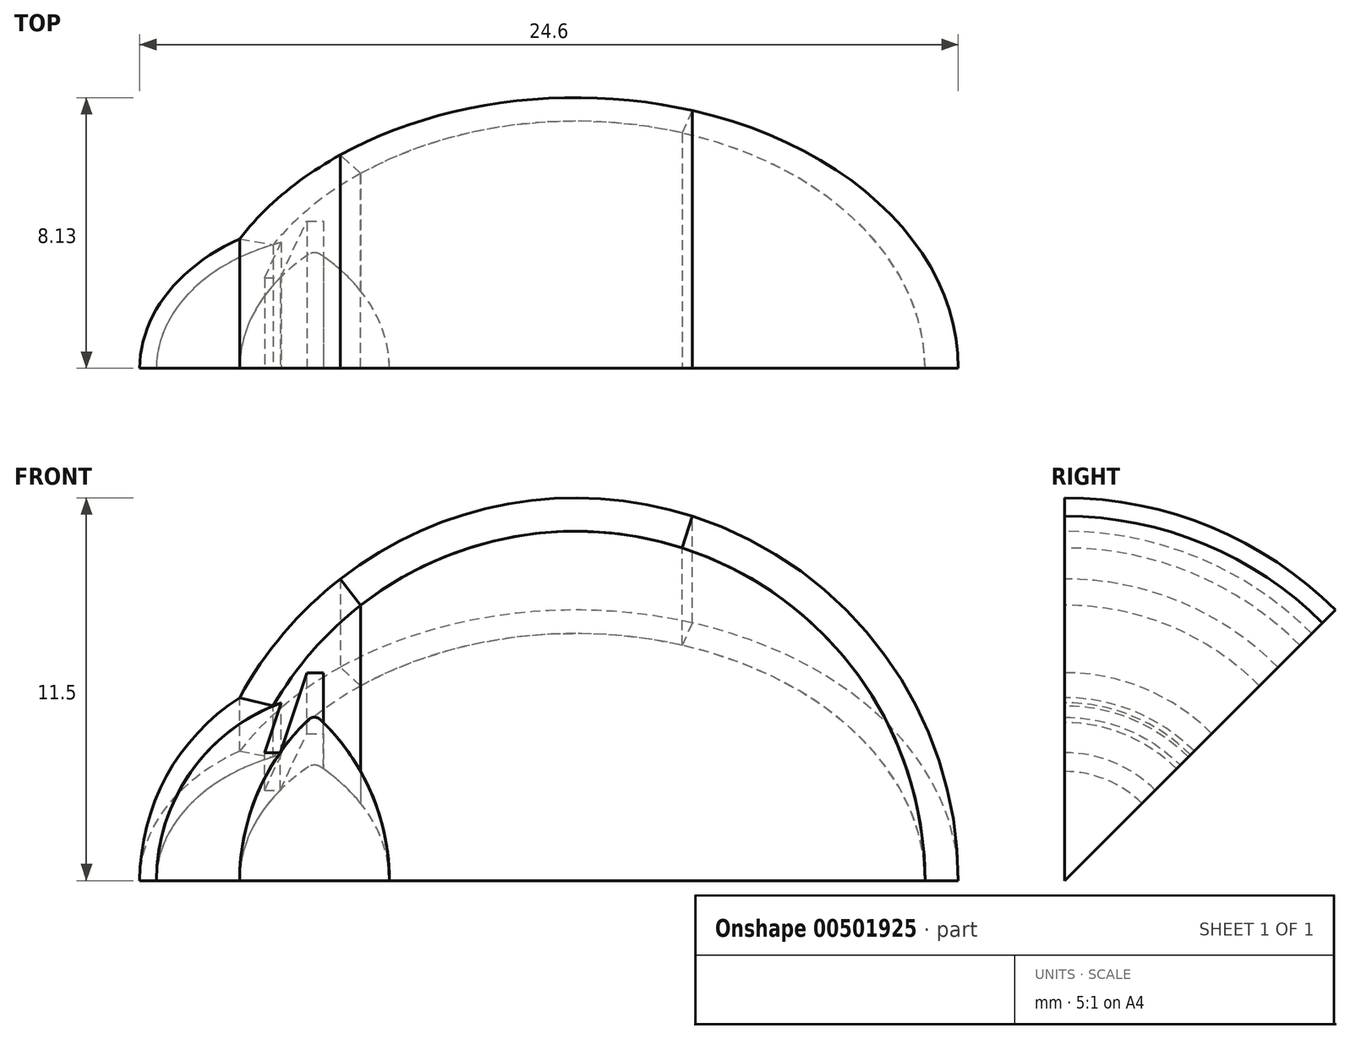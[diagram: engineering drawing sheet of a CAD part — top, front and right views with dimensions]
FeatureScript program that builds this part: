
annotation { "Feature Type Name" : "Feature", "Feature Type Description" : "" }
export const myFeature = defineFeature(function(context is Context, id is Id, definition is map)
    precondition{}
    {
        {
            var Q0;
            Q0=qCreatedBy(makeId("Front.planeOp"),FACE);
            var sketch = newSketch(context, id + "F0", { "sketchPlane" : qUnion([Q0])});
            skArc(sketch, "E0", {"start": v(11.5, 0) * mm, "mid": v(2.84, 11.14) * mm, "end": v(-10.1, 5.5) * mm});
            skLineSegment(sketch, "E1", {"start": v(11.5, 0) * mm, "end": v(-11.5, 0) * mm});
            skArc(sketch, "E2", {"start": v(-10.1, 5.5) * mm, "mid": v(-12.3, 3.13) * mm, "end": v(-13.1, 0) * mm});
            skLineSegment(sketch, "E3", {"start": v(-11.5, 0) * mm, "end": v(-13.1, 0) * mm});
            skSolve(sketch);
        }
        {
            var Q0;
            Q0=qSketchRegion(id+"F0",true);
            var Q1;
            Q1=sQuery(id+"F0.wireOp",EDGE,"E1");
            revolve(context, id + "F1", {"entities" : qUnion([Q0]), "axis" : qUnion([Q1]), "revolveType" : RevolveType.ONE_DIRECTION, "angle" : 45 * degree});
        }
        {
            var Q0;
            Q0=qCreatedBy(makeId("Front.planeOp"),FACE);
            var sketch = newSketch(context, id + "F2", { "sketchPlane" : qUnion([Q0])});
            skLineSegment(sketch, "E4", {"start": v(-10.1, 5.5) * mm, "end": v(-9.1, 5.25) * mm});
            skLineSegment(sketch, "E5", {"start": v(11.5, 0) * mm, "end": v(10.5, 0) * mm});
            skArc(sketch, "E6", {"start": v(10.5, 0) * mm, "mid": v(2.72, 10.14) * mm, "end": v(-9.1, 5.25) * mm});
            skArc(sketch, "E7", {"start": v(11.5, 0) * mm, "mid": v(2.84, 11.14) * mm, "end": v(-10.1, 5.5) * mm});
            skSolve(sketch);
        }
        {
            var Q0;
            Q0=makeQuery(id+"F2.imprint","IMPRINT",FACE,{"disambiguationData":[TD([[makeQuery(id+"F2.imprint","IMPRINT",EDGE,{"derivedFrom":sQuery(id+"F2.wireOp",EDGE,"E4")}),1.0]])]});
            var Q1;
            Q1=sQuery(id+"F2.wireOp",EDGE,"E6");
            var Q2;
            Q2=sQuery(id+"F2.wireOp",EDGE,"E4");
            var Q3;
            Q3=sQuery(id+"F0.wireOp",EDGE,"E1");
            revolve(context, id + "F3", {"operationType" : NewBodyOperationType.REMOVE, "entities" : qUnion([Q0]), "surfaceEntities" : qUnion([Q1, Q2]), "axis" : qUnion([Q3]), "revolveType" : RevolveType.ONE_DIRECTION, "angle" : 45 * degree});
        }
        {
            var Q0;
            Q0=qSketchRegion(id+"F2",true);
            var Q1;
            Q1=sQuery(id+"F0.wireOp",EDGE,"E1");
            revolve(context, id + "F4", {"entities" : qUnion([Q0]), "axis" : qUnion([Q1]), "revolveType" : RevolveType.ONE_DIRECTION, "angle" : 45 * degree});
        }
        {
            var Q0;
            Q0=makeQuery(id+"F0.imprint","IMPRINT",FACE,{"disambiguationData":[TD([[makeQuery(id+"F0.imprint","IMPRINT",EDGE,{"derivedFrom":sQuery(id+"F0.wireOp",EDGE,"E0")}),1.0]])]});
            var sketch = newSketch(context, id + "F5", { "sketchPlane" : qUnion([Q0])});
            skArc(sketch, "E8", {"start": v(-9.1, 5.25) * mm, "mid": v(-11.64, 3.16) * mm, "end": v(-12.6, 0) * mm});
            skLineSegment(sketch, "E9", {"start": v(-10.1, 5.5) * mm, "end": v(-9.1, 5.25) * mm});
            skLineSegment(sketch, "E10", {"start": v(-13.1, 0) * mm, "end": v(-12.6, 0) * mm});
            skArc(sketch, "E11", {"start": v(-10.1, 5.5) * mm, "mid": v(-12.3, 3.13) * mm, "end": v(-13.1, 0) * mm});
            skSolve(sketch);
        }
        {
            var Q0;
            Q0=qSketchRegion(id+"F5",true);
            var Q1;
            Q1=sQuery(id+"F5.wireOp",EDGE,"E8");
            var Q2;
            Q2=sQuery(id+"F5.wireOp",EDGE,"E9");
            var Q3;
            Q3=sQuery(id+"F0.wireOp",EDGE,"E3");
            revolve(context, id + "F6", {"operationType" : NewBodyOperationType.REMOVE, "entities" : qUnion([Q0]), "surfaceEntities" : qUnion([Q1, Q2]), "axis" : qUnion([Q3]), "revolveType" : RevolveType.ONE_DIRECTION, "angle" : 45 * degree});
        }
        {
            var Q0;
            Q0=qSketchRegion(id+"F5",true);
            var Q1;
            Q1=sQuery(id+"F0.wireOp",EDGE,"E1");
            revolve(context, id + "F7", {"entities" : qUnion([Q0]), "axis" : qUnion([Q1]), "revolveType" : RevolveType.ONE_DIRECTION, "angle" : 45 * degree});
        }
        {
            var Q0;
            Q0=qCreatedBy(makeId("Front.planeOp"),FACE);
            var sketch = newSketch(context, id + "F8", { "sketchPlane" : qUnion([Q0])});
            skArc(sketch, "E12", {"start": v(10, 0) * mm, "mid": v(8.28, 6.14) * mm, "end": v(3.2, 10) * mm});
            skLineSegment(sketch, "E13", {"start": v(10, 0) * mm, "end": v(10.5, 0) * mm});
            skArc(sketch, "E14", {"start": v(10.5, 0) * mm, "mid": v(8.48, 6.2) * mm, "end": v(3.2, 10) * mm});
            skSolve(sketch);
        }
        {
            var Q0;
            Q0=qSketchRegion(id+"F8",true);
            var Q1;
            Q1=sQuery(id+"F8.wireOp",EDGE,"E12");
            var Q2;
            Q2=sQuery(id+"F0.wireOp",EDGE,"E1");
            revolve(context, id + "F9", {"operationType" : NewBodyOperationType.REMOVE, "entities" : qUnion([Q0]), "surfaceEntities" : qUnion([Q1]), "axis" : qUnion([Q2]), "revolveType" : RevolveType.ONE_DIRECTION, "angle" : 45 * degree});
        }
        {
            var Q0;
            Q0=qSketchRegion(id+"F8",true);
            var Q1;
            Q1=sQuery(id+"F8.wireOp",EDGE,"E13");
            revolve(context, id + "F10", {"entities" : qUnion([Q0]), "axis" : qUnion([Q1]), "revolveType" : RevolveType.ONE_DIRECTION, "oppositeDirection" : true, "angle" : 45 * degree});
        }
        {
            var Q0;
            Q0=makeQuery(id+"F0.imprint","IMPRINT",FACE,{"disambiguationData":[TD([[makeQuery(id+"F0.imprint","IMPRINT",EDGE,{"derivedFrom":sQuery(id+"F0.wireOp",EDGE,"E0")}),1.0]])]});
            var sketch = newSketch(context, id + "F11", { "sketchPlane" : qUnion([Q0])});
            skLineSegment(sketch, "E15", {"start": v(8.35, 0) * mm, "end": v(9.86, 0) * mm});
            skLineSegment(sketch, "E16", {"start": v(9.86, 0) * mm, "end": v(9.86, 2.23) * mm});
            skLineSegment(sketch, "E17", {"start": v(9.86, 2.23) * mm, "end": v(8.35, 2.23) * mm});
            skLineSegment(sketch, "E18", {"start": v(8.35, 2.23) * mm, "end": v(8.35, 0) * mm});
            skSolve(sketch);
        }
        {
            var Q0;
            Q0=qSketchRegion(id+"F11",true);
            var Q1;
            Q1=sQuery(id+"F11.wireOp",EDGE,"E15");
            revolve(context, id + "F12", {"operationType" : NewBodyOperationType.REMOVE, "entities" : qUnion([Q0]), "axis" : qUnion([Q1]), "revolveType" : RevolveType.ONE_DIRECTION, "oppositeDirection" : true, "angle" : 45 * degree});
        }
        {
            var Q0;
            Q0=qSketchRegion(id+"F11",true);
            var Q1;
            Q1=sQuery(id+"F0.wireOp",EDGE,"E1");
            revolve(context, id + "F13", {"entities" : qUnion([Q0]), "axis" : qUnion([Q1]), "revolveType" : RevolveType.ONE_DIRECTION, "angle" : 45 * degree});
        }
        {
            var Q0;
            Q0=qCreatedBy(makeId("Front.planeOp"),FACE);
            var sketch = newSketch(context, id + "F14", { "sketchPlane" : qUnion([Q0])});
            skLineSegment(sketch, "E19", {"start": v(9.86, 2.23) * mm, "end": v(9.86, 0) * mm});
            skLineSegment(sketch, "E20", {"start": v(9.86, 0) * mm, "end": v(10, 0) * mm});
            skArc(sketch, "E21", {"start": v(10, 0) * mm, "mid": v(10, 1.12) * mm, "end": v(9.86, 2.23) * mm});
            skSolve(sketch);
        }
        {
            var Q0;
            Q0=qSketchRegion(id+"F14",true);
            var Q1;
            Q1=sQuery(id+"F14.wireOp",EDGE,"E20");
            revolve(context, id + "F15", {"operationType" : NewBodyOperationType.REMOVE, "entities" : qUnion([Q0]), "axis" : qUnion([Q1]), "revolveType" : RevolveType.ONE_DIRECTION, "oppositeDirection" : true, "angle" : 45 * degree});
        }
        {
            var Q0;
            Q0=qSketchRegion(id+"F14",true);
            var Q1;
            Q1=sQuery(id+"F0.wireOp",EDGE,"E1");
            revolve(context, id + "F16", {"operationType" : NewBodyOperationType.ADD, "entities" : qUnion([Q0]), "axis" : qUnion([Q1]), "revolveType" : RevolveType.ONE_DIRECTION, "angle" : 45 * degree});
        }
        {
            var Q0;
            Q0=qCreatedBy(makeId("Front.planeOp"),FACE);
            var sketch = newSketch(context, id + "F17", { "sketchPlane" : qUnion([Q0])});
            skLineSegment(sketch, "E22", {"start": v(3.5, 10.95) * mm, "end": v(3.2, 10) * mm});
            skArc(sketch, "E23", {"start": v(10.5, 0) * mm, "mid": v(8.48, 6.2) * mm, "end": v(3.2, 10) * mm});
            skArc(sketch, "E24", {"start": v(11.5, 0) * mm, "mid": v(9.29, 6.78) * mm, "end": v(3.5, 10.95) * mm});
            skLineSegment(sketch, "E25", {"start": v(10.5, 0) * mm, "end": v(11.5, 0) * mm});
            skSolve(sketch);
        }
        {
            var Q0;
            Q0 = qSketchRegion(id + "F17", true);
            var Q1;
            Q1=sQuery(id+"F17.wireOp",EDGE,"E25");
            revolve(context, id + "F18", {"operationType" : NewBodyOperationType.REMOVE, "entities" : qUnion([Q0]), "axis" : qUnion([Q1]), "revolveType" : RevolveType.FULL, "oppositeDirection" : true});
        }
        {
            var Q0;
            Q0 = qSketchRegion(id + "F17", true);
            var Q1;
            Q1=sQuery(id+"F0.wireOp",EDGE,"E1");
            revolve(context, id + "F19", {"entities" : qUnion([Q0]), "axis" : qUnion([Q1]), "revolveType" : RevolveType.ONE_DIRECTION, "angle" : 45 * degree});
        }
        {
            var Q0;
            Q0=qCreatedBy(makeId("Front.planeOp"),FACE);
            var sketch = newSketch(context, id + "F20", { "sketchPlane" : qUnion([Q0])});
            skArc(sketch, "E26", {"start": v(-8.85, 5.34) * mm, "mid": v(-11.57, 3.26) * mm, "end": v(-12.6, 0) * mm});
            skLineSegment(sketch, "E27", {"start": v(-8.85, 5.34) * mm, "end": v(-9.35, 3.84) * mm});
            skLineSegment(sketch, "E28", {"start": v(-9.35, 3.84) * mm, "end": v(-8.85, 3.84) * mm});
            skLineSegment(sketch, "E29", {"start": v(-12.6, 0) * mm, "end": v(-8.85, 0) * mm});
            skLineSegment(sketch, "E30", {"start": v(-8.85, 3.84) * mm, "end": v(-8.85, 0) * mm});
            skSolve(sketch);
        }
        {
            var Q0;
            Q0 = qSketchRegion(id + "F20", true);
            var Q1;
            Q1=sQuery(id+"F20.wireOp",EDGE,"E29");
            revolve(context, id + "F21", {"operationType" : NewBodyOperationType.REMOVE, "entities" : qUnion([Q0]), "axis" : qUnion([Q1]), "revolveType" : RevolveType.FULL, "oppositeDirection" : true});
        }
        {
            var Q0;
            Q0 = qSketchRegion(id + "F20", true);
            var Q1;
            Q1=sQuery(id+"F0.wireOp",EDGE,"E1");
            revolve(context, id + "F22", {"entities" : qUnion([Q0]), "axis" : qUnion([Q1]), "revolveType" : RevolveType.ONE_DIRECTION, "angle" : 45 * degree});
        }
        {
            var Q0;
            Q0=qCreatedBy(makeId("Front.planeOp"),FACE);
            var sketch = newSketch(context, id + "F23", { "sketchPlane" : qUnion([Q0])});
            skLineSegment(sketch, "E31", {"start": v(-11.42, 10.2) * mm, "end": v(-11.42, 10.2) * mm});
            skLineSegment(sketch, "E32", {"start": v(-5.6, 0) * mm, "end": v(-10.1, 0) * mm});
            skArc(sketch, "E33", {"start": v(-8.02, 4.84) * mm, "mid": v(-9.56, 2.63) * mm, "end": v(-10.1, 0) * mm});
            skLineSegment(sketch, "E34", {"start": v(-8.1, 0) * mm, "end": v(-8.1, 4.77) * mm, "construction": true});
            skArc(sketch, "E35", {"start": v(-5.6, 0) * mm, "mid": v(-6.14, 2.63) * mm, "end": v(-7.68, 4.84) * mm});
            skPoint(sketch, "E36.visualSharp", {"position": v(-7.85, 5) * mm});
            skArc(sketch, "E36.filletArc", {"start": v(-7.68, 4.84) * mm, "mid": v(-7.85, 4.91) * mm, "end": v(-8.02, 4.84) * mm});
            skSolve(sketch);
        }
        {
            var Q0;
            Q0 = qSketchRegion(id + "F23", true);
            var Q1;
            Q1=sQuery(id+"F0.wireOp",EDGE,"E1");
            revolve(context, id + "F24", {"operationType" : NewBodyOperationType.REMOVE, "entities" : qUnion([Q0]), "axis" : qUnion([Q1]), "revolveType" : RevolveType.FULL, "oppositeDirection" : true});
        }
        {
            var Q0;
            Q0 = qSketchRegion(id + "F23", true);
            var Q1;
            Q1=sQuery(id+"F0.wireOp",EDGE,"E1");
            revolve(context, id + "F25", {"entities" : qUnion([Q0]), "axis" : qUnion([Q1]), "revolveType" : RevolveType.ONE_DIRECTION, "angle" : 45 * degree});
        }
        {
            var Q0;
            Q0=qCreatedBy(makeId("Front.planeOp"),FACE);
            var sketch = newSketch(context, id + "F26", { "sketchPlane" : qUnion([Q0])});
            skLineSegment(sketch, "E37", {"start": v(-9.35, 3.84) * mm, "end": v(-8.88, 3.84) * mm});
            skLineSegment(sketch, "E38", {"start": v(-8.88, 3.84) * mm, "end": v(-8.08, 6.25) * mm});
            skLineSegment(sketch, "E39", {"start": v(-8.08, 6.25) * mm, "end": v(-7.58, 6.25) * mm});
            skLineSegment(sketch, "E40", {"start": v(-7.58, 6.25) * mm, "end": v(-7.58, 4.75) * mm});
            skLineSegment(sketch, "E41", {"start": v(-6.46, 3.28) * mm, "end": v(-6.46, 8.28) * mm});
            skLineSegment(sketch, "E42", {"start": v(-9.35, 3.84) * mm, "end": v(-8.85, 5.34) * mm});
            skArc(sketch, "E43", {"start": v(-6.46, 8.28) * mm, "mid": v(-7.92, 6.9) * mm, "end": v(-9.1, 5.25) * mm});
            skArc(sketch, "E44", {"start": v(-8.85, 5.34) * mm, "mid": v(-8.97, 5.3) * mm, "end": v(-9.1, 5.25) * mm});
            skArc(sketch, "E45", {"start": v(-6.46, 3.28) * mm, "mid": v(-6.97, 4.05) * mm, "end": v(-7.58, 4.75) * mm});
            skSolve(sketch);
        }
        {
            var Q0;
            Q0 = qSketchRegion(id + "F26", true);
            var Q1;
            Q1=sQuery(id+"F23.wireOp",EDGE,"E32");
            revolve(context, id + "F27", {"operationType" : NewBodyOperationType.REMOVE, "entities" : qUnion([Q0]), "axis" : qUnion([Q1]), "revolveType" : RevolveType.FULL, "oppositeDirection" : true});
        }
        {
            var Q0;
            Q0 = qSketchRegion(id + "F26", true);
            var Q1;
            Q1=sQuery(id+"F23.wireOp",EDGE,"E32");
            revolve(context, id + "F28", {"entities" : qUnion([Q0]), "axis" : qUnion([Q1]), "revolveType" : RevolveType.ONE_DIRECTION, "angle" : 45 * degree});
        }
        {
            var Q0;
            Q0=qCreatedBy(makeId("Front.planeOp"),FACE);
            var sketch = newSketch(context, id + "F29", { "sketchPlane" : qUnion([Q0])});
            skLineSegment(sketch, "E46", {"start": v(-6.46, 8.28) * mm, "end": v(-7.07, 9.07) * mm});
            skArc(sketch, "E47", {"start": v(-7.07, 9.07) * mm, "mid": v(-8.77, 7.44) * mm, "end": v(-10.1, 5.5) * mm});
            skArc(sketch, "E48", {"start": v(-6.46, 8.28) * mm, "mid": v(-7.92, 6.9) * mm, "end": v(-9.1, 5.25) * mm});
            skPoint(sketch, "E48.second.point", {"position": v(-9.1, 5.25) * mm});
            skPoint(sketch, "E48.third.point", {"position": v(-6.46, 8.28) * mm});
            skLineSegment(sketch, "E49", {"start": v(-10.1, 5.5) * mm, "end": v(-9.1, 5.25) * mm});
            skSolve(sketch);
        }
        {
            var Q0;
            Q0 = qSketchRegion(id + "F29", true);
            var Q1;
            Q1=sQuery(id+"F23.wireOp",EDGE,"E32");
            revolve(context, id + "F30", {"operationType" : NewBodyOperationType.REMOVE, "entities" : qUnion([Q0]), "axis" : qUnion([Q1]), "revolveType" : RevolveType.FULL, "oppositeDirection" : true});
        }
        {
            var Q0;
            Q0 = qSketchRegion(id + "F29", true);
            var Q1;
            Q1=sQuery(id+"F23.wireOp",EDGE,"E32");
            revolve(context, id + "F31", {"entities" : qUnion([Q0]), "axis" : qUnion([Q1]), "revolveType" : RevolveType.ONE_DIRECTION, "angle" : 45 * degree});
        }
    });
